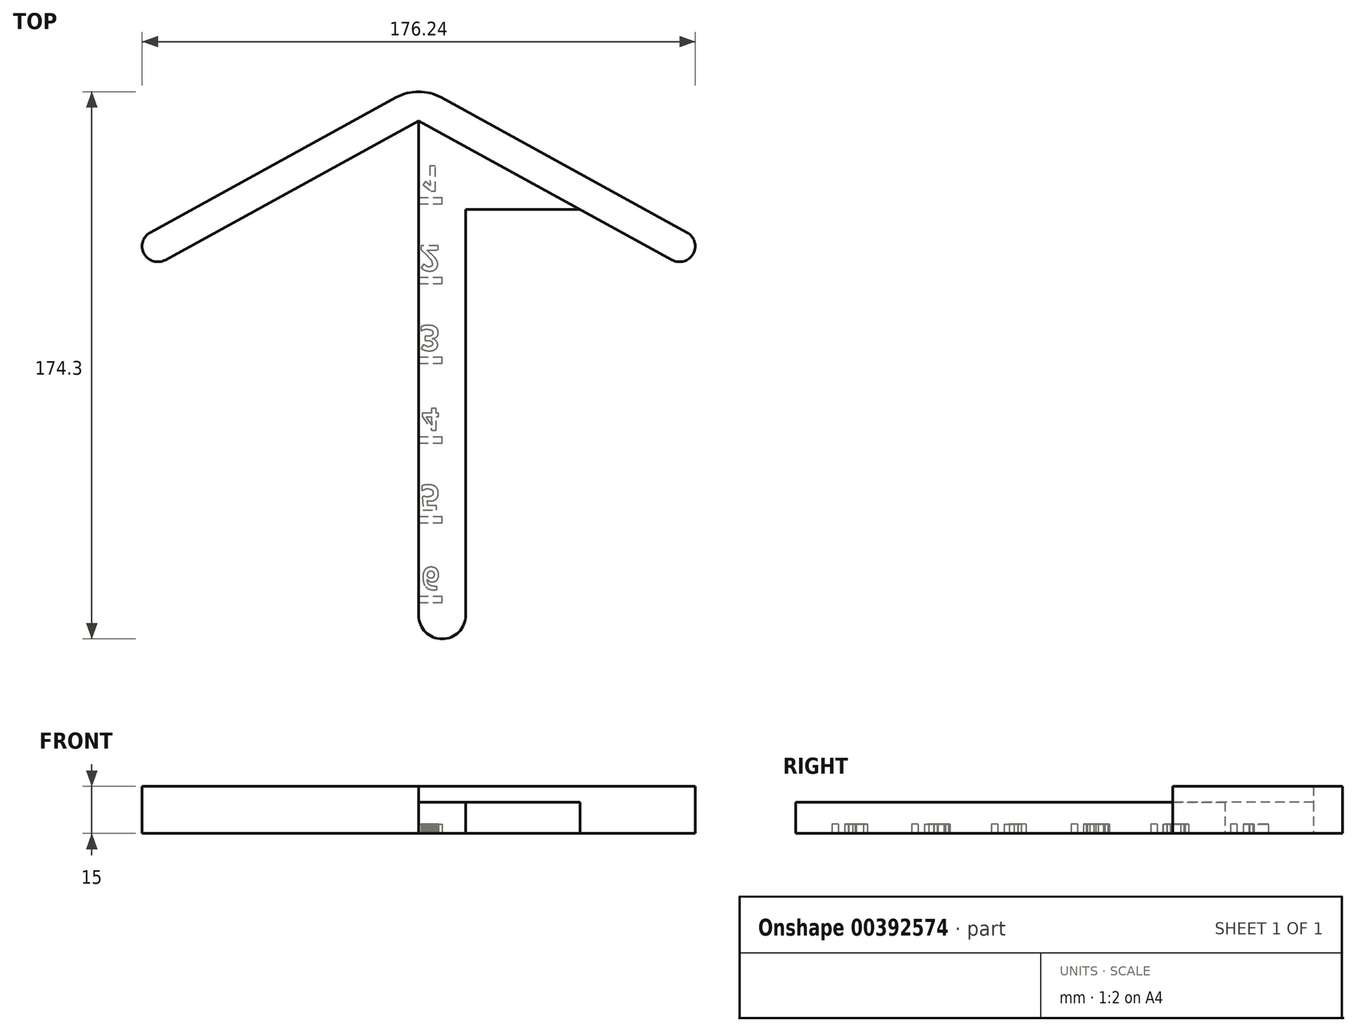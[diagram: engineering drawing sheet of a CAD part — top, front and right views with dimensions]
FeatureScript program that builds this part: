
annotation { "Feature Type Name" : "Feature", "Feature Type Description" : "" }
export const myFeature = defineFeature(function(context is Context, id is Id, definition is map)
    precondition{}
    {
        {
            var Q0;
            Q0=qCreatedBy(makeId("Top.planeOp"),FACE);
            var sketch = newSketch(context, id + "F0", { "sketchPlane" : qUnion([Q0])});
            skLineSegment(sketch, "E0", {"start": v(-90, 0) * mm, "end": v(0, 49.38) * mm});
            skLineSegment(sketch, "E1", {"start": v(0, 49.38) * mm, "end": v(90, 0) * mm});
            skLineSegment(sketch, "E2", {"start": v(90, 0) * mm, "end": v(85, -8.66) * mm});
            skLineSegment(sketch, "E3", {"start": v(85, -8.66) * mm, "end": v(0, 37.97) * mm});
            skLineSegment(sketch, "E4", {"start": v(0, 37.97) * mm, "end": v(-85, -8.66) * mm});
            skLineSegment(sketch, "E5", {"start": v(-85, -8.66) * mm, "end": v(-90, 0) * mm});
            skSolve(sketch);
        }
        {
            var Q0;
            Q0=qCreatedBy(makeId("Top.planeOp"),FACE);
            var sketch = newSketch(context, id + "F1", { "sketchPlane" : qUnion([Q0])});
            skLineSegment(sketch, "E6", {"start": v(0, 37.97) * mm, "end": v(0, -127.03) * mm});
            skLineSegment(sketch, "E7", {"start": v(0, -127.03) * mm, "end": v(15, -127.03) * mm});
            skLineSegment(sketch, "E8", {"start": v(15, -127.03) * mm, "end": v(15, 29.74) * mm});
            skLineSegment(sketch, "E9", {"start": v(15, 9.74) * mm, "end": v(51.46, 9.74) * mm});
            skLineSegment(sketch, "E10", {"start": v(0, 37.97) * mm, "end": v(51.46, 9.74) * mm});
            skSolve(sketch);
        }
        {
            var Q0;
            Q0=makeQuery(id+"F0.imprint","IMPRINT",FACE,{"disambiguationData":[TD([[makeQuery(id+"F0.imprint","IMPRINT",EDGE,{"derivedFrom":sQuery(id+"F0.wireOp",EDGE,"E0")}),-1.0]])]});
            extrude(context, id + "F2", {"entities" : qUnion([Q0]), "depth" : 15 * mm});
        }
        {
            var Q0;
            {var subQ5=sQuery(id+"F1.wireOp",EDGE,"E6");Q0=makeQuery(id+"F1.imprint","IMPRINT",FACE,{"disambiguationData":[TD([[makeQuery(id+"F1.imprint","IMPRINT",EDGE,{"derivedFrom":subQ5}),1.0]])]});}
            var Q1;
            {var subQ3=sQuery(id+"F1.wireOp",EDGE,"E9");Q1=makeQuery(id+"F1.imprint","IMPRINT",FACE,{"disambiguationData":[TD([[makeQuery(id+"F1.imprint","IMPRINT",EDGE,{"derivedFrom":subQ3}),1.0]])]});}
            extrude(context, id + "F3", {"entities" : qUnion([Q0, Q1]), "operationType" : NewBodyOperationType.ADD, "depth" : 10 * mm});
        }
        {
            var Q0;
            Q0=makeQuery(id+"F3.opExtrude","SWEPT_EDGE",EDGE,{"disambiguationData":[OSD([sQuery(id+"F1.wireOp",EDGE,"E6"),sQuery(id+"F1.wireOp",EDGE,"E7")])]});
            var Q1;
            Q1=makeQuery(id+"F3.opExtrude","SWEPT_EDGE",EDGE,{"disambiguationData":[OSD([sQuery(id+"F1.wireOp",EDGE,"E7"),sQuery(id+"F1.wireOp",EDGE,"E8")])]});
            fillet(context, id + "F4", {"entities" : qUnion([Q0, Q1]), "radius" : 7.5 * mm, "tangentPropagation" : true, "allowEdgeOverflow" : false});
        }
        {
            var Q0;
            Q0=makeQuery(id+"F2.opExtrude","SWEPT_EDGE",EDGE,{"disambiguationData":[OSD([sQuery(id+"F0.wireOp",EDGE,"E0"),sQuery(id+"F0.wireOp",EDGE,"E5")])]});
            var Q1;
            Q1=makeQuery(id+"F2.opExtrude","SWEPT_EDGE",EDGE,{"disambiguationData":[OSD([sQuery(id+"F0.wireOp",EDGE,"E4"),sQuery(id+"F0.wireOp",EDGE,"E5")])]});
            var Q2;
            Q2=makeQuery(id+"F2.opExtrude","SWEPT_EDGE",EDGE,{"disambiguationData":[OSD([sQuery(id+"F0.wireOp",EDGE,"E1"),sQuery(id+"F0.wireOp",EDGE,"E2")])]});
            var Q3;
            Q3=makeQuery(id+"F2.opExtrude","SWEPT_EDGE",EDGE,{"disambiguationData":[OSD([sQuery(id+"F0.wireOp",EDGE,"E2"),sQuery(id+"F0.wireOp",EDGE,"E3")])]});
            fillet(context, id + "F5", {"entities" : qUnion([Q0, Q1, Q2, Q3]), "radius" : 5 * mm, "tangentPropagation" : true, "allowEdgeOverflow" : false});
        }
        {
            var Q0;
            Q0=makeQuery(id+"F2.opExtrude","SWEPT_EDGE",EDGE,{"disambiguationData":[OSD([sQuery(id+"F0.wireOp",EDGE,"E0"),sQuery(id+"F0.wireOp",EDGE,"E1")])]});
            fillet(context, id + "F6", {"entities" : qUnion([Q0]), "radius" : 15 * mm, "tangentPropagation" : true, "allowEdgeOverflow" : false});
        }
        {
            var Q0;
            Q0=makeQuery(id+"F3.boolean.opBoolean","MERGE",FACE,{"derivedFrom":[makeQuery(id+"F2.opExtrude","CAP_FACE",FACE,{"disambiguationData":[OSD([sQuery(id+"F0.wireOp",EDGE,"E0"),sQuery(id+"F0.wireOp",EDGE,"E1"),sQuery(id+"F0.wireOp",EDGE,"E2"),sQuery(id+"F0.wireOp",EDGE,"E3"),sQuery(id+"F0.wireOp",EDGE,"E4"),sQuery(id+"F0.wireOp",EDGE,"E5")])],"isStart":true}),makeQuery(id+"F3.opExtrude","CAP_FACE",FACE,{"disambiguationData":[OSD([sQuery(id+"F1.wireOp",EDGE,"E6"),sQuery(id+"F1.wireOp",EDGE,"E7"),sQuery(id+"F1.wireOp",EDGE,"E8"),sQuery(id+"F1.wireOp",EDGE,"E9"),sQuery(id+"F1.wireOp",EDGE,"E10")])],"isStart":true})]});
            var sketch = newSketch(context, id + "F7", { "sketchPlane" : qUnion([Q0])});
            skPoint(sketch, "E11", {"position": v(0, -11.57) * mm});
            skPoint(sketch, "E12", {"position": v(0, 13.83) * mm});
            skPoint(sketch, "E13", {"position": v(0, 39.23) * mm});
            skPoint(sketch, "E14", {"position": v(0, 64.63) * mm});
            skPoint(sketch, "E15", {"position": v(0, 90.03) * mm});
            skPoint(sketch, "E16", {"position": v(0, 115.43) * mm});
            skLineSegment(sketch, "E17.bottom", {"start": v(0, -11.57) * mm, "end": v(7.5, -11.57) * mm});
            skLineSegment(sketch, "E17.top", {"start": v(0, -13.57) * mm, "end": v(7.5, -13.57) * mm});
            skLineSegment(sketch, "E17.left", {"start": v(0, -11.57) * mm, "end": v(0, -13.57) * mm});
            skLineSegment(sketch, "E17.right", {"start": v(7.5, -11.57) * mm, "end": v(7.5, -13.57) * mm});
            skLineSegment(sketch, "E18.bottom", {"start": v(0, 13.83) * mm, "end": v(7.5, 13.83) * mm});
            skLineSegment(sketch, "E18.top", {"start": v(0, 11.83) * mm, "end": v(7.5, 11.83) * mm});
            skLineSegment(sketch, "E18.left", {"start": v(0, 13.83) * mm, "end": v(0, 11.83) * mm});
            skLineSegment(sketch, "E18.right", {"start": v(7.5, 13.83) * mm, "end": v(7.5, 11.83) * mm});
            skLineSegment(sketch, "E19.bottom", {"start": v(0, 39.23) * mm, "end": v(7.5, 39.23) * mm});
            skLineSegment(sketch, "E19.top", {"start": v(0, 37.23) * mm, "end": v(7.5, 37.23) * mm});
            skLineSegment(sketch, "E19.left", {"start": v(0, 39.23) * mm, "end": v(0, 37.23) * mm});
            skLineSegment(sketch, "E19.right", {"start": v(7.5, 39.23) * mm, "end": v(7.5, 37.23) * mm});
            skLineSegment(sketch, "E20.bottom", {"start": v(0, 64.63) * mm, "end": v(7.5, 64.63) * mm});
            skLineSegment(sketch, "E20.top", {"start": v(0, 62.63) * mm, "end": v(7.5, 62.63) * mm});
            skLineSegment(sketch, "E20.left", {"start": v(0, 64.63) * mm, "end": v(0, 62.63) * mm});
            skLineSegment(sketch, "E20.right", {"start": v(7.5, 64.63) * mm, "end": v(7.5, 62.63) * mm});
            skLineSegment(sketch, "E21.bottom", {"start": v(0, 90.03) * mm, "end": v(7.5, 90.03) * mm});
            skLineSegment(sketch, "E21.top", {"start": v(0, 88.03) * mm, "end": v(7.5, 88.03) * mm});
            skLineSegment(sketch, "E21.left", {"start": v(0, 90.03) * mm, "end": v(0, 88.03) * mm});
            skLineSegment(sketch, "E21.right", {"start": v(7.5, 90.03) * mm, "end": v(7.5, 88.03) * mm});
            skLineSegment(sketch, "E22.bottom", {"start": v(0, 115.43) * mm, "end": v(7.5, 115.43) * mm});
            skLineSegment(sketch, "E22.top", {"start": v(0, 113.43) * mm, "end": v(7.5, 113.43) * mm});
            skLineSegment(sketch, "E22.left", {"start": v(0, 115.43) * mm, "end": v(0, 113.43) * mm});
            skLineSegment(sketch, "E22.right", {"start": v(7.5, 115.43) * mm, "end": v(7.5, 113.43) * mm});
            skPoint(sketch, "E23", {"position": v(7.5, 3.83) * mm});
            skPoint(sketch, "E24", {"position": v(7.5, 29.23) * mm});
            skPoint(sketch, "E25", {"position": v(7.5, 54.63) * mm});
            skPoint(sketch, "E26", {"position": v(7.5, 80.03) * mm});
            skPoint(sketch, "E27", {"position": v(7.5, 105.43) * mm});
            skPoint(sketch, "E28", {"position": v(7.5, -21.57) * mm});
            skSolve(sketch);
        }
        {
            var Q0;
            Q0=makeQuery(id+"F7.imprint","IMPRINT",FACE,{"disambiguationData":[TD([[makeQuery(id+"F7.imprint","IMPRINT",EDGE,{"derivedFrom":sQuery(id+"F7.wireOp",EDGE,"E17.bottom")}),-1.0]])]});
            var Q1;
            Q1=makeQuery(id+"F7.imprint","IMPRINT",FACE,{"disambiguationData":[TD([[makeQuery(id+"F7.imprint","IMPRINT",EDGE,{"derivedFrom":sQuery(id+"F7.wireOp",EDGE,"E18.bottom")}),-1.0]])]});
            var Q2;
            Q2=makeQuery(id+"F7.imprint","IMPRINT",FACE,{"disambiguationData":[TD([[makeQuery(id+"F7.imprint","IMPRINT",EDGE,{"derivedFrom":sQuery(id+"F7.wireOp",EDGE,"E19.bottom")}),-1.0]])]});
            var Q3;
            Q3=makeQuery(id+"F7.imprint","IMPRINT",FACE,{"disambiguationData":[TD([[makeQuery(id+"F7.imprint","IMPRINT",EDGE,{"derivedFrom":sQuery(id+"F7.wireOp",EDGE,"E20.bottom")}),-1.0]])]});
            var Q4;
            Q4=makeQuery(id+"F7.imprint","IMPRINT",FACE,{"disambiguationData":[TD([[makeQuery(id+"F7.imprint","IMPRINT",EDGE,{"derivedFrom":sQuery(id+"F7.wireOp",EDGE,"E21.bottom")}),-1.0]])]});
            var Q5;
            Q5=makeQuery(id+"F7.imprint","IMPRINT",FACE,{"disambiguationData":[TD([[makeQuery(id+"F7.imprint","IMPRINT",EDGE,{"derivedFrom":sQuery(id+"F7.wireOp",EDGE,"E22.bottom")}),-1.0]])]});
            extrude(context, id + "F8", {"entities" : qUnion([Q0, Q1, Q2, Q3, Q4, Q5]), "operationType" : NewBodyOperationType.REMOVE, "oppositeDirection" : true, "depth" : 3 * mm});
        }
        {
            var Q0;
            Q0=makeQuery(id+"F3.boolean.opBoolean","MERGE",FACE,{"derivedFrom":[makeQuery(id+"F2.opExtrude","CAP_FACE",FACE,{"disambiguationData":[OSD([sQuery(id+"F0.wireOp",EDGE,"E0"),sQuery(id+"F0.wireOp",EDGE,"E1"),sQuery(id+"F0.wireOp",EDGE,"E2"),sQuery(id+"F0.wireOp",EDGE,"E3"),sQuery(id+"F0.wireOp",EDGE,"E4"),sQuery(id+"F0.wireOp",EDGE,"E5")])],"isStart":true}),makeQuery(id+"F3.opExtrude","CAP_FACE",FACE,{"disambiguationData":[OSD([sQuery(id+"F1.wireOp",EDGE,"E6"),sQuery(id+"F1.wireOp",EDGE,"E7"),sQuery(id+"F1.wireOp",EDGE,"E8"),sQuery(id+"F1.wireOp",EDGE,"E9"),sQuery(id+"F1.wireOp",EDGE,"E10")])],"isStart":true})]});
            var sketch = newSketch(context, id + "F9", { "sketchPlane" : qUnion([Q0])});
            skPoint(sketch, "E29", {"position": v(7.5, -21.57) * mm});
            skPoint(sketch, "E30", {"position": v(7.5, 3.83) * mm});
            skPoint(sketch, "E31", {"position": v(7.5, 29.23) * mm});
            skPoint(sketch, "E32", {"position": v(7.5, 54.63) * mm});
            skPoint(sketch, "E33", {"position": v(7.5, 80.03) * mm});
            skPoint(sketch, "E34", {"position": v(7.5, 105.43) * mm});
            skSolve(sketch);
        }
        {
            var Q0;
            {var subQ8=sQuery(id+"F1.wireOp",EDGE,"E9");Q0=makeQuery(id+"F9.imprint","IMPRINT",FACE,{"disambiguationData":[TD([[makeQuery(id+"F9.imprint","IMPRINT",EDGE,{"derivedFrom":makeQuery(id+"F3.opExtrude","CAP_EDGE",EDGE,{"disambiguationData":[OSD([subQ8])],"isStart":true})}),-1.0]])]});}
            var sketch = newSketch(context, id + "F10", { "sketchPlane" : qUnion([Q0])});
            skText(sketch, "E35", { "text": "6", "fontName": "OpenSans-Bold.ttf"});
            const initialGuessF10  = {"E35": [0.001, 0.10428, 1, 0, 0.00715]};
            skSetInitialGuess(sketch, initialGuessF10);
            skSolve(sketch);
        }
        {
            var Q0;
            {var subQ8=sQuery(id+"F1.wireOp",EDGE,"E9");Q0=makeQuery(id+"F9.imprint","IMPRINT",FACE,{"disambiguationData":[TD([[makeQuery(id+"F9.imprint","IMPRINT",EDGE,{"derivedFrom":makeQuery(id+"F3.opExtrude","CAP_EDGE",EDGE,{"disambiguationData":[OSD([subQ8])],"isStart":true})}),-1.0]])]});}
            var sketch = newSketch(context, id + "F11", { "sketchPlane" : qUnion([Q0])});
            skText(sketch, "E36", { "text": "4", "fontName": "OpenSans-Bold.ttf"});
            const initialGuessF11  = {"E36": [0.001, 0.05366, 1, 0, 0.00697]};
            skSetInitialGuess(sketch, initialGuessF11);
            skSolve(sketch);
        }
        {
            var Q0;
            {var subQ8=sQuery(id+"F1.wireOp",EDGE,"E9");Q0=makeQuery(id+"F9.imprint","IMPRINT",FACE,{"disambiguationData":[TD([[makeQuery(id+"F9.imprint","IMPRINT",EDGE,{"derivedFrom":makeQuery(id+"F3.opExtrude","CAP_EDGE",EDGE,{"disambiguationData":[OSD([subQ8])],"isStart":true})}),-1.0]])]});}
            var sketch = newSketch(context, id + "F12", { "sketchPlane" : qUnion([Q0])});
            skText(sketch, "E37", { "text": "3", "fontName": "OpenSans-Bold.ttf"});
            const initialGuessF12  = {"E37": [0.00037, 0.02723, 1, 0, 0.008]};
            skSetInitialGuess(sketch, initialGuessF12);
            skSolve(sketch);
        }
        {
            var Q0;
            {var subQ8=sQuery(id+"F1.wireOp",EDGE,"E9");Q0=makeQuery(id+"F9.imprint","IMPRINT",FACE,{"disambiguationData":[TD([[makeQuery(id+"F9.imprint","IMPRINT",EDGE,{"derivedFrom":makeQuery(id+"F3.opExtrude","CAP_EDGE",EDGE,{"disambiguationData":[OSD([subQ8])],"isStart":true})}),-1.0]])]});}
            var sketch = newSketch(context, id + "F13", { "sketchPlane" : qUnion([Q0])});
            skText(sketch, "E38", { "text": "2", "fontName": "OpenSans-Bold.ttf"});
            const initialGuessF13  = {"E38": [0.00029, 0.00183, 1, 0, 0.008]};
            skSetInitialGuess(sketch, initialGuessF13);
            skSolve(sketch);
        }
        {
            var Q0;
            {var subQ8=sQuery(id+"F1.wireOp",EDGE,"E9");Q0=makeQuery(id+"F9.imprint","IMPRINT",FACE,{"disambiguationData":[TD([[makeQuery(id+"F9.imprint","IMPRINT",EDGE,{"derivedFrom":makeQuery(id+"F3.opExtrude","CAP_EDGE",EDGE,{"disambiguationData":[OSD([subQ8])],"isStart":true})}),-1.0]])]});}
            var sketch = newSketch(context, id + "F14", { "sketchPlane" : qUnion([Q0])});
            skText(sketch, "E39", { "text": "1", "fontName": "OpenSans-Bold.ttf"});
            const initialGuessF14  = {"E39": [0.00069, -0.02357, 1, 0, 0.008]};
            skSetInitialGuess(sketch, initialGuessF14);
            skSolve(sketch);
        }
        {
            var Q0;
            {var subQ8=sQuery(id+"F1.wireOp",EDGE,"E9");Q0=makeQuery(id+"F9.imprint","IMPRINT",FACE,{"disambiguationData":[TD([[makeQuery(id+"F9.imprint","IMPRINT",EDGE,{"derivedFrom":makeQuery(id+"F3.opExtrude","CAP_EDGE",EDGE,{"disambiguationData":[OSD([subQ8])],"isStart":true})}),-1.0]])]});}
            var sketch = newSketch(context, id + "F15", { "sketchPlane" : qUnion([Q0])});
            skText(sketch, "E40", { "text": "5", "fontName": "OpenSans-Bold.ttf"});
            const initialGuessF15  = {"E40": [0.00044, 0.07803, 1, 0, 0.008]};
            skSetInitialGuess(sketch, initialGuessF15);
            skSolve(sketch);
        }
        {
            var Q0;
            Q0 = qSketchRegion(id + "F10", true);
            var Q1;
            Q1 = qSketchRegion(id + "F15", true);
            var Q2;
            Q2 = qSketchRegion(id + "F11", true);
            var Q3;
            Q3 = qSketchRegion(id + "F12", true);
            var Q4;
            Q4 = qSketchRegion(id + "F13", true);
            var Q5;
            Q5 = qSketchRegion(id + "F14", true);
            extrude(context, id + "F16", {"entities" : qUnion([Q0, Q1, Q2, Q3, Q4, Q5]), "operationType" : NewBodyOperationType.REMOVE, "oppositeDirection" : true, "depth" : 3 * mm});
        }
    });
